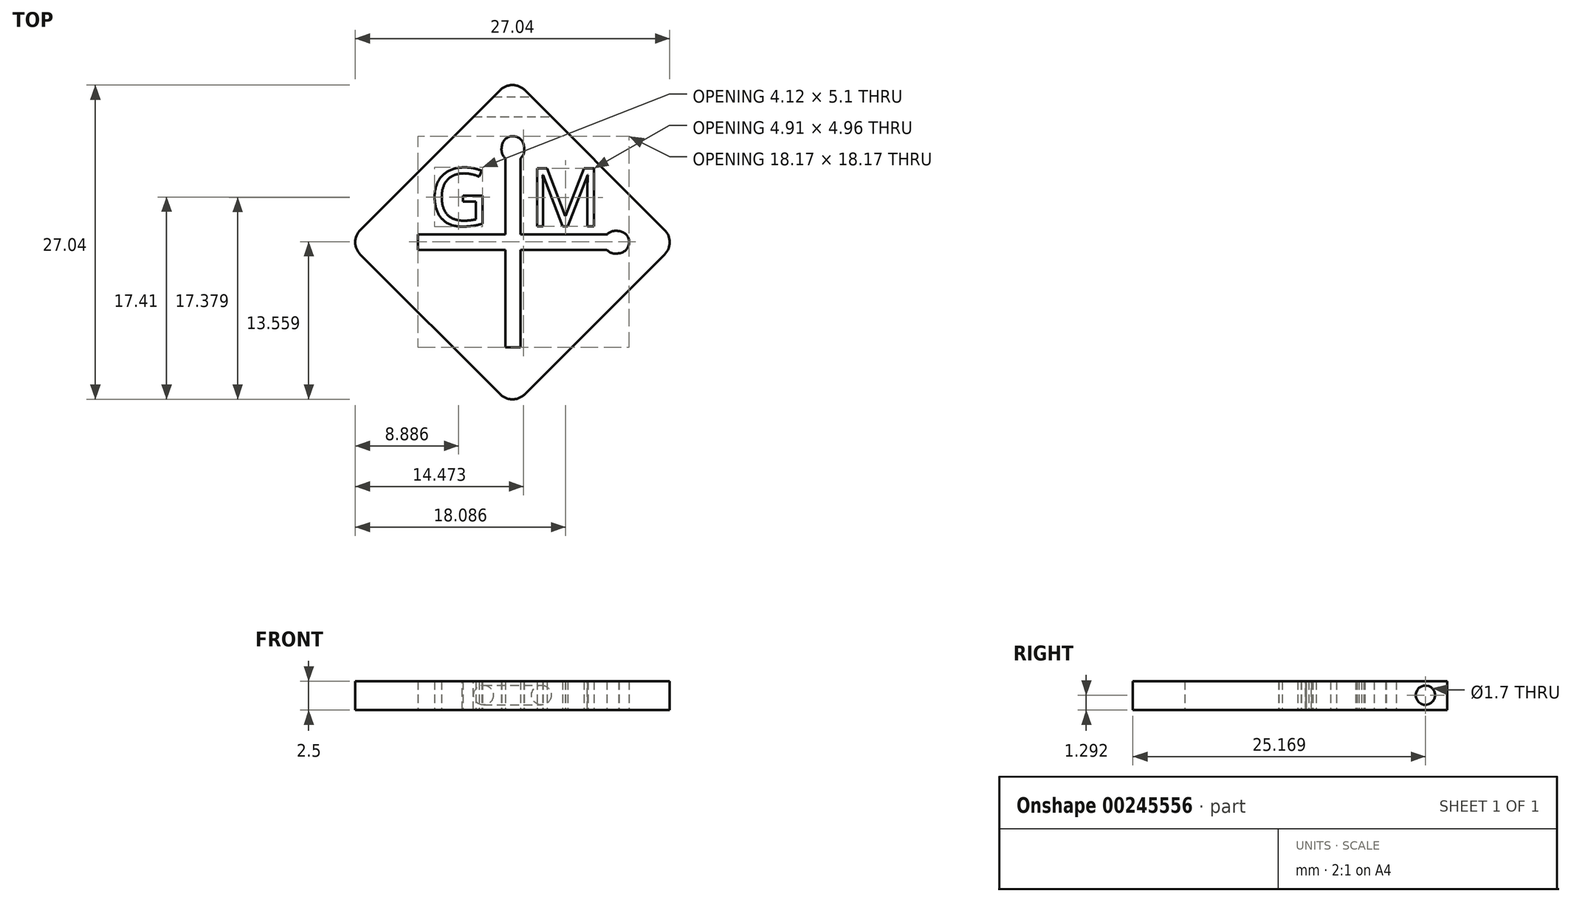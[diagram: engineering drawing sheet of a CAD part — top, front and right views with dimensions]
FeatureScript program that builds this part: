
annotation { "Feature Type Name" : "Feature", "Feature Type Description" : "" }
export const myFeature = defineFeature(function(context is Context, id is Id, definition is map)
    precondition{}
    {
        {
            var Q0;
            Q0=qCreatedBy(makeId("Top.planeOp"),FACE);
            var sketch = newSketch(context, id + "F0", { "sketchPlane" : qUnion([Q0])});
            skLineSegment(sketch, "E0", {"start": v(1.06, -1.06) * mm, "end": v(13.08, -13.08) * mm});
            skLineSegment(sketch, "E1", {"start": v(13.08, -15.2) * mm, "end": v(1.06, -27.22) * mm});
            skLineSegment(sketch, "E2", {"start": v(-1.06, -27.22) * mm, "end": v(-13.08, -15.2) * mm});
            skLineSegment(sketch, "E3", {"start": v(-13.08, -13.08) * mm, "end": v(-1.06, -1.06) * mm});
            skPoint(sketch, "E4.visualSharp", {"position": v(0, 0) * mm});
            skArc(sketch, "E4.filletArc", {"start": v(1.06, -1.06) * mm, "mid": v(0, -0.62) * mm, "end": v(-1.06, -1.06) * mm});
            skPoint(sketch, "E5.visualSharp", {"position": v(-14.14, -14.14) * mm});
            skArc(sketch, "E5.filletArc", {"start": v(-13.08, -13.08) * mm, "mid": v(-13.52, -14.14) * mm, "end": v(-13.08, -15.2) * mm});
            skPoint(sketch, "E6.visualSharp", {"position": v(14.14, -14.14) * mm});
            skArc(sketch, "E6.filletArc", {"start": v(13.08, -15.2) * mm, "mid": v(13.52, -14.14) * mm, "end": v(13.08, -13.08) * mm});
            skPoint(sketch, "E7.visualSharp", {"position": v(0, -28.28) * mm});
            skArc(sketch, "E7.filletArc", {"start": v(-1.06, -27.22) * mm, "mid": v(0, -27.66) * mm, "end": v(1.06, -27.22) * mm});
            skLineSegment(sketch, "E8", {"start": v(0, 0) * mm, "end": v(0, -31.86) * mm, "construction": true});
            skLineSegment(sketch, "E9", {"start": v(-14.14, -14.14) * mm, "end": v(14.14, -14.14) * mm, "construction": true});
            skLineSegment(sketch, "E10", {"start": v(-8.13, -13.48) * mm, "end": v(-8.13, -14.8) * mm});
            skLineSegment(sketch, "E11", {"start": v(-8.13, -14.8) * mm, "end": v(8.13, -14.8) * mm});
            skLineSegment(sketch, "E12", {"start": v(8.13, -13.48) * mm, "end": v(-8.13, -13.48) * mm});
            skLineSegment(sketch, "E13", {"start": v(-8.13, -13.48) * mm, "end": v(0, -13.48) * mm, "construction": true});
            skLineSegment(sketch, "E14", {"start": v(0, -13.48) * mm, "end": v(8.13, -13.48) * mm, "construction": true});
            skArc(sketch, "E15", {"start": v(9.18, -15.1) * mm, "mid": v(10.04, -14.12) * mm, "end": v(9.13, -13.2) * mm});
            skArc(sketch, "E16", {"start": v(9.13, -13.2) * mm, "mid": v(8.6, -13.2) * mm, "end": v(8.13, -13.48) * mm});
            skArc(sketch, "E17", {"start": v(8.13, -14.8) * mm, "mid": v(8.61, -15.1) * mm, "end": v(9.18, -15.1) * mm});
            skLineSegment(sketch, "E18", {"start": v(-0.62, -23.19) * mm, "end": v(0.7, -23.19) * mm});
            skLineSegment(sketch, "E19", {"start": v(0.7, -23.19) * mm, "end": v(0.7, -6.92) * mm});
            skLineSegment(sketch, "E20", {"start": v(-0.62, -6.92) * mm, "end": v(-0.62, -23.19) * mm});
            skLineSegment(sketch, "E21", {"start": v(-0.62, -23.19) * mm, "end": v(-0.62, -15.05) * mm, "construction": true});
            skLineSegment(sketch, "E22", {"start": v(-0.62, -15.05) * mm, "end": v(-0.62, -6.92) * mm, "construction": true});
            skArc(sketch, "E23", {"start": v(0.99, -5.88) * mm, "mid": v(0.02, -5.01) * mm, "end": v(-0.91, -5.92) * mm});
            skArc(sketch, "E24", {"start": v(-0.91, -5.92) * mm, "mid": v(-0.9, -6.46) * mm, "end": v(-0.62, -6.92) * mm});
            skArc(sketch, "E25", {"start": v(0.7, -6.92) * mm, "mid": v(1, -6.44) * mm, "end": v(0.99, -5.88) * mm});
            skText(sketch, "E26", { "text": "G", "fontName": "OpenSans-Regular.ttf"});
            skText(sketch, "E27", { "text": "M", "fontName": "OpenSans-Regular.ttf"});
            const initialGuessF0  = {"E26": [-0.00712, -0.01273, 1, 0, 0.005], "E27": [0.00143, -0.01276, 1, 0, 0.005]};
            skSetInitialGuess(sketch, initialGuessF0);
            skSolve(sketch);
        }
        {
            var Q0;
            Q0=makeQuery(id+"F0.imprint","IMPRINT",FACE,{"disambiguationData":[TD([[makeQuery(id+"F0.imprint","IMPRINT",EDGE,{"derivedFrom":sQuery(id+"F0.wireOp",EDGE,"E0")}),-1.0]])]});
            extrude(context, id + "F1", {"entities" : qUnion([Q0]), "depth" : 2.5 * mm});
        }
        {
            var Q0;
            Q0=qCreatedBy(makeId("Right.planeOp"),FACE);
            var sketch = newSketch(context, id + "F2", { "sketchPlane" : qUnion([Q0])});
            skCircle(sketch, "E28", {"center": v(-2.5, 1.3) * mm, "radius": 0.85 * mm});
            skSolve(sketch);
        }
        {
            var Q0;
            Q0=qSketchRegion(id+"F2",true);
            extrude(context, id + "F3", {"entities" : qUnion([Q0]), "operationType" : NewBodyOperationType.REMOVE, "endBound" : BoundingType.SYMMETRIC, "oppositeDirection" : true, "depth" : 25 * mm});
        }
    });
